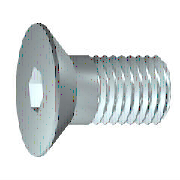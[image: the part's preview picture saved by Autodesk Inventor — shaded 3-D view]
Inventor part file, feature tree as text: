
AUTODESK INVENTOR PART (.ipt)
format: ipt  version: 2020 (Build 240168000, 168)  size: 177,664 bytes
history: native  units: mm (DEFAULTED — no unit token found)
features: sketch x2, extrude x1, plane x1
ambient origin geometry x7: Origin, YZ Plane, XY Plane, X Axis, Y Axis, Z Axis, Center Point
bodies: Solid1 (feature_tree), Body (feature_tree)
feature tree (4):
  sketch  "Sketch2"  dims[d2=1.5mm d3=4.0mm d6=2.48mm d7=45.0deg d8=2.886751mm d9=60.0deg d10=7.53mm d11=4.0mm d12=0.429415mm d13=90.0deg d30=10.0mm d14=0.0mm d15=20.0mm d16=0.0mm d17=0.429415mm d18=0.429415mm d20=0.0mm d39=45.0deg d43=0.0mm d44=0.0mm]
  extrude  "Slot"  Depth=20.0mm
  plane  "Work Plane1"
  sketch  "Sketch1"  dims[d0=45.0mm d1=20.0mm]
